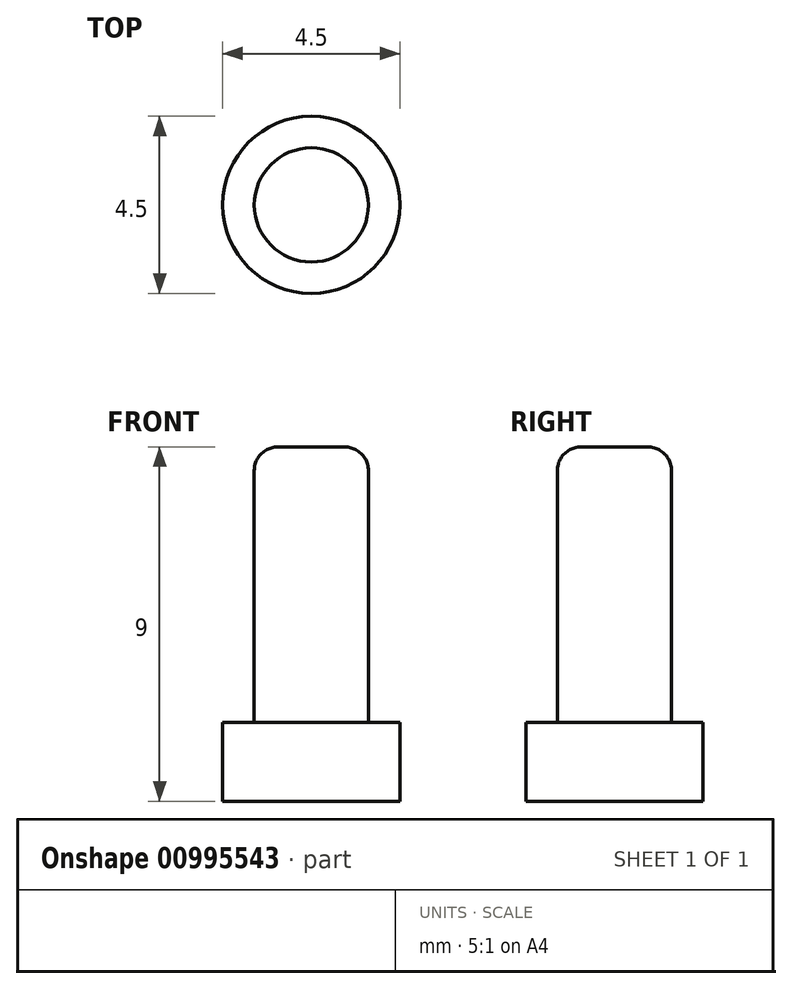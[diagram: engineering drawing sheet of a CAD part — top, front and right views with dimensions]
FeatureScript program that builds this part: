
annotation { "Feature Type Name" : "Feature", "Feature Type Description" : "" }
export const myFeature = defineFeature(function(context is Context, id is Id, definition is map)
    precondition{}
    {
        {
            var Q0;
            Q0=qCreatedBy(makeId("Top.planeOp"),FACE);
            var sketch = newSketch(context, id + "F0", { "sketchPlane" : qUnion([Q0])});
            skCircle(sketch, "E0", {"center": v(0, 0) * mm, "radius": 2.25 * mm});
            skSolve(sketch);
        }
        {
            var Q0;
            Q0=makeQuery(id+"F0.imprint","IMPRINT",FACE,{"disambiguationData":[TD([[makeQuery(id+"F0.imprint","IMPRINT",EDGE,{"derivedFrom":sQuery(id+"F0.wireOp",EDGE,"E0")}),1.0]])]});
            extrude(context, id + "F1", {"entities" : qUnion([Q0]), "depth" : 2 * mm, "offsetDistance" : 25 * mm});
        }
        {
            var Q0;
            Q0=makeQuery(id+"F1.opExtrude","CAP_FACE",FACE,{"disambiguationData":[OSD([sQuery(id+"F0.wireOp",EDGE,"E0")])],"isStart":false});
            var sketch = newSketch(context, id + "F2", { "sketchPlane" : qUnion([Q0])});
            skCircle(sketch, "E1", {"center": v(0, 0) * mm, "radius": 1.45 * mm});
            skSolve(sketch);
        }
        {
            var Q0;
            Q0=makeQuery(id+"F2.imprint","IMPRINT",FACE,{"disambiguationData":[TD([[makeQuery(id+"F2.imprint","IMPRINT",EDGE,{"derivedFrom":sQuery(id+"F2.wireOp",EDGE,"E1")}),1.0]])]});
            extrude(context, id + "F3", {"entities" : qUnion([Q0]), "operationType" : NewBodyOperationType.ADD, "depth" : 7 * mm, "offsetDistance" : 25 * mm});
        }
        {
            var Q0;
            Q0=makeQuery(id+"F3.opExtrude","CAP_EDGE",EDGE,{"disambiguationData":[OSD([sQuery(id+"F2.wireOp",EDGE,"E1")])],"isStart":false});
            fillet(context, id + "F4", {"entities" : qUnion([Q0]), "radius" : .6 * mm, "tangentPropagation" : true, "allowEdgeOverflow" : false});
        }
    });
